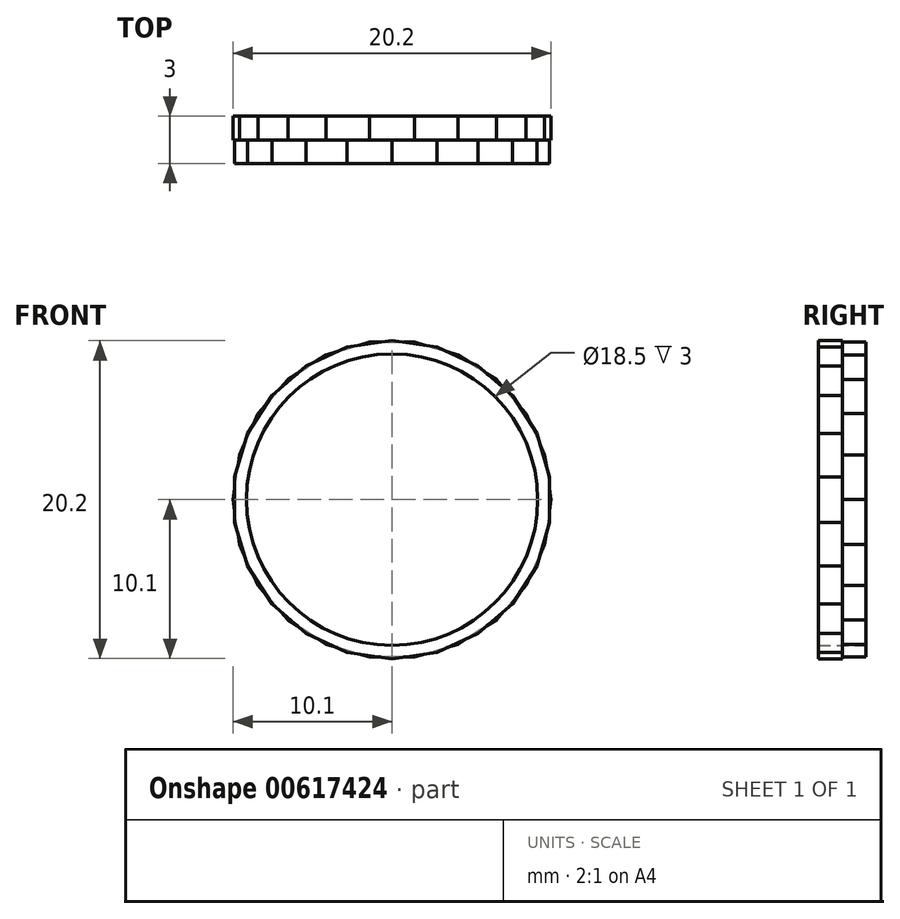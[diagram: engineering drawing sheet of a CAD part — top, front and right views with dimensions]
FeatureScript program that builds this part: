
annotation { "Feature Type Name" : "Feature", "Feature Type Description" : "" }
export const myFeature = defineFeature(function(context is Context, id is Id, definition is map)
    precondition{}
    {
        {
            var Q0;
            Q0=qCreatedBy(makeId("Front.planeOp"),FACE);
            var sketch = newSketch(context, id + "F0", { "sketchPlane" : qUnion([Q0])});
            skCircle(sketch, "E0.cCircle", {"center": v(0, 0) * mm, "radius": 10 * mm, "construction": true});
            skLineSegment(sketch, "E0.0", {"start": v(4.2, 9.19) * mm, "end": v(6.62, 7.64) * mm});
            skLineSegment(sketch, "E0.1", {"start": v(6.62, 7.64) * mm, "end": v(8.5, 5.46) * mm});
            skLineSegment(sketch, "E0.2", {"start": v(8.5, 5.46) * mm, "end": v(9.7, 2.85) * mm});
            skLineSegment(sketch, "E0.3", {"start": v(9.7, 2.85) * mm, "end": v(10.1, 0) * mm});
            skLineSegment(sketch, "E0.4", {"start": v(10.1, 0) * mm, "end": v(9.7, -2.85) * mm});
            skLineSegment(sketch, "E0.5", {"start": v(9.7, -2.85) * mm, "end": v(8.5, -5.46) * mm});
            skLineSegment(sketch, "E0.6", {"start": v(8.5, -5.46) * mm, "end": v(6.62, -7.64) * mm});
            skLineSegment(sketch, "E0.7", {"start": v(6.62, -7.64) * mm, "end": v(4.2, -9.19) * mm});
            skLineSegment(sketch, "E0.8", {"start": v(4.2, -9.19) * mm, "end": v(1.44, -10) * mm});
            skLineSegment(sketch, "E0.9", {"start": v(1.44, -10) * mm, "end": v(-1.44, -10) * mm});
            skLineSegment(sketch, "E0.10", {"start": v(-1.44, -10) * mm, "end": v(-4.2, -9.19) * mm});
            skLineSegment(sketch, "E0.11", {"start": v(-4.2, -9.19) * mm, "end": v(-6.62, -7.64) * mm});
            skLineSegment(sketch, "E0.12", {"start": v(-6.62, -7.64) * mm, "end": v(-8.5, -5.46) * mm});
            skLineSegment(sketch, "E0.13", {"start": v(-8.5, -5.46) * mm, "end": v(-9.7, -2.85) * mm});
            skLineSegment(sketch, "E0.14", {"start": v(-9.7, -2.85) * mm, "end": v(-10.1, 0) * mm});
            skLineSegment(sketch, "E0.15", {"start": v(-10.1, 0) * mm, "end": v(-9.7, 2.85) * mm});
            skLineSegment(sketch, "E0.16", {"start": v(-9.7, 2.85) * mm, "end": v(-8.5, 5.46) * mm});
            skLineSegment(sketch, "E0.17", {"start": v(-8.5, 5.46) * mm, "end": v(-6.62, 7.64) * mm});
            skLineSegment(sketch, "E0.18", {"start": v(-6.62, 7.64) * mm, "end": v(-4.2, 9.19) * mm});
            skLineSegment(sketch, "E0.19", {"start": v(-4.2, 9.19) * mm, "end": v(-1.44, 10) * mm});
            skLineSegment(sketch, "E0.20", {"start": v(-1.44, 10) * mm, "end": v(1.44, 10) * mm});
            skLineSegment(sketch, "E0.21", {"start": v(1.44, 10) * mm, "end": v(4.2, 9.19) * mm});
            skPoint(sketch, "E0.0.midPoint", {"position": v(5.4, 8.41) * mm});
            skCircle(sketch, "E1", {"center": v(0, 0) * mm, "radius": 9.25 * mm});
            skSolve(sketch);
        }
        {
            var Q0;
            Q0 = qSketchRegion(id + "F0", true);
            extrude(context, id + "F1", {"entities" : qUnion([Q0]), "depth" : 1.5 * mm, "offsetDistance" : 25 * mm});
        }
        {
            var Q0;
            Q0=makeQuery(id+"F1.opExtrude","CAP_FACE",FACE,{"disambiguationData":[OSD([sQuery(id+"F0.wireOp",EDGE,"E0.0"),sQuery(id+"F0.wireOp",EDGE,"E0.1"),sQuery(id+"F0.wireOp",EDGE,"E0.2"),sQuery(id+"F0.wireOp",EDGE,"E0.3"),sQuery(id+"F0.wireOp",EDGE,"E0.4"),sQuery(id+"F0.wireOp",EDGE,"E0.5"),sQuery(id+"F0.wireOp",EDGE,"E0.6"),sQuery(id+"F0.wireOp",EDGE,"E0.7"),sQuery(id+"F0.wireOp",EDGE,"E0.8"),sQuery(id+"F0.wireOp",EDGE,"E0.9"),sQuery(id+"F0.wireOp",EDGE,"E0.10"),sQuery(id+"F0.wireOp",EDGE,"E0.11"),sQuery(id+"F0.wireOp",EDGE,"E0.12"),sQuery(id+"F0.wireOp",EDGE,"E0.13"),sQuery(id+"F0.wireOp",EDGE,"E0.14"),sQuery(id+"F0.wireOp",EDGE,"E0.15"),sQuery(id+"F0.wireOp",EDGE,"E0.16"),sQuery(id+"F0.wireOp",EDGE,"E0.17"),sQuery(id+"F0.wireOp",EDGE,"E0.18"),sQuery(id+"F0.wireOp",EDGE,"E0.19"),sQuery(id+"F0.wireOp",EDGE,"E0.20"),sQuery(id+"F0.wireOp",EDGE,"E0.21"),sQuery(id+"F0.wireOp",EDGE,"E1")])],"isStart":false});
            var sketch = newSketch(context, id + "F2", { "sketchPlane" : qUnion([Q0])});
            skCircle(sketch, "E2.cCircle", {"center": v(0, 0) * mm, "radius": 10 * mm, "construction": true});
            skLineSegment(sketch, "E2.0", {"start": v(2.85, 9.7) * mm, "end": v(5.46, 8.5) * mm});
            skLineSegment(sketch, "E2.1", {"start": v(5.46, 8.5) * mm, "end": v(7.64, 6.62) * mm});
            skLineSegment(sketch, "E2.2", {"start": v(7.64, 6.62) * mm, "end": v(9.19, 4.2) * mm});
            skLineSegment(sketch, "E2.3", {"start": v(9.19, 4.2) * mm, "end": v(10, 1.44) * mm});
            skLineSegment(sketch, "E2.4", {"start": v(10, 1.44) * mm, "end": v(10, -1.44) * mm});
            skLineSegment(sketch, "E2.5", {"start": v(10, -1.44) * mm, "end": v(9.19, -4.2) * mm});
            skLineSegment(sketch, "E2.6", {"start": v(9.19, -4.2) * mm, "end": v(7.64, -6.62) * mm});
            skLineSegment(sketch, "E2.7", {"start": v(7.64, -6.62) * mm, "end": v(5.46, -8.5) * mm});
            skLineSegment(sketch, "E2.8", {"start": v(5.46, -8.5) * mm, "end": v(2.85, -9.7) * mm});
            skLineSegment(sketch, "E2.9", {"start": v(2.85, -9.7) * mm, "end": v(0, -10.1) * mm});
            skLineSegment(sketch, "E2.10", {"start": v(0, -10.1) * mm, "end": v(-2.85, -9.7) * mm});
            skLineSegment(sketch, "E2.11", {"start": v(-2.85, -9.7) * mm, "end": v(-5.46, -8.5) * mm});
            skLineSegment(sketch, "E2.12", {"start": v(-5.46, -8.5) * mm, "end": v(-7.64, -6.62) * mm});
            skLineSegment(sketch, "E2.13", {"start": v(-7.64, -6.62) * mm, "end": v(-9.19, -4.2) * mm});
            skLineSegment(sketch, "E2.14", {"start": v(-9.19, -4.2) * mm, "end": v(-10, -1.44) * mm});
            skLineSegment(sketch, "E2.15", {"start": v(-10, -1.44) * mm, "end": v(-10, 1.44) * mm});
            skLineSegment(sketch, "E2.16", {"start": v(-10, 1.44) * mm, "end": v(-9.19, 4.2) * mm});
            skLineSegment(sketch, "E2.17", {"start": v(-9.19, 4.2) * mm, "end": v(-7.64, 6.62) * mm});
            skLineSegment(sketch, "E2.18", {"start": v(-7.64, 6.62) * mm, "end": v(-5.46, 8.5) * mm});
            skLineSegment(sketch, "E2.19", {"start": v(-5.46, 8.5) * mm, "end": v(-2.85, 9.7) * mm});
            skLineSegment(sketch, "E2.20", {"start": v(-2.85, 9.7) * mm, "end": v(0, 10.1) * mm});
            skLineSegment(sketch, "E2.21", {"start": v(0, 10.1) * mm, "end": v(2.85, 9.7) * mm});
            skPoint(sketch, "E2.0.midPoint", {"position": v(4.15, 9.1) * mm});
            skCircle(sketch, "E3", {"center": v(0, 0) * mm, "radius": 9.25 * mm});
            skSolve(sketch);
        }
        {
            var Q0;
            Q0 = qSketchRegion(id + "F2", true);
            extrude(context, id + "F3", {"entities" : qUnion([Q0]), "operationType" : NewBodyOperationType.ADD, "depth" : 1.5 * mm, "offsetDistance" : 25 * mm});
        }
    });
